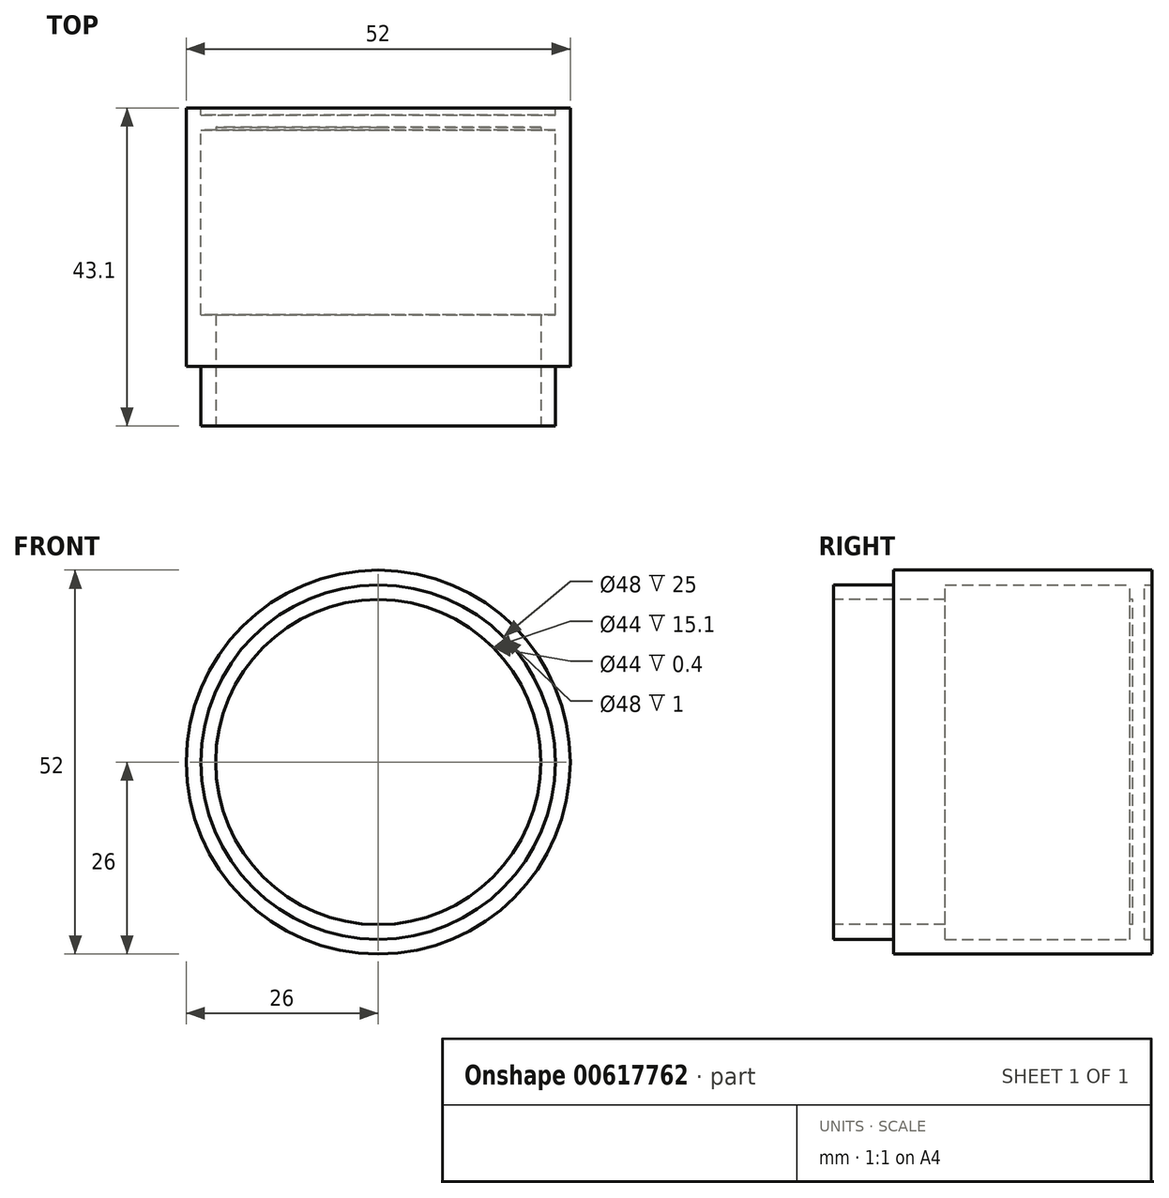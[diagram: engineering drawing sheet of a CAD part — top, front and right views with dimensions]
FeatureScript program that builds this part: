
annotation { "Feature Type Name" : "Feature", "Feature Type Description" : "" }
export const myFeature = defineFeature(function(context is Context, id is Id, definition is map)
    precondition{}
    {
        {
            var Q0;
            Q0=qCreatedBy(makeId("Front.planeOp"),FACE);
            var sketch = newSketch(context, id + "F0", { "sketchPlane" : qUnion([Q0])});
            skArc(sketch, "E0", {"start": v(-25.92, -2) * mm, "mid": v(0, -26) * mm, "end": v(25.92, -2) * mm});
            skCircle(sketch, "E1", {"center": v(0, 0) * mm, "radius": 24 * mm});
            skArc(sketch, "E2.trimOffspring", {"start": v(25.92, 2) * mm, "mid": v(0, 26) * mm, "end": v(-25.92, 2) * mm});
            skArc(sketch, "E3", {"start": v(25.92, -2) * mm, "mid": v(26, 0) * mm, "end": v(25.92, 2) * mm});
            skPoint(sketch, "E4.MirrorCS.end.orphan", {"position": v(26.83, -2) * mm});
            skPoint(sketch, "E4.MirrorCS.start.orphan", {"position": v(26.83, 2) * mm});
            skArc(sketch, "E5.trimOffspring", {"start": v(-25.92, 2) * mm, "mid": v(-26, 0) * mm, "end": v(-25.92, -2) * mm});
            skPoint(sketch, "E6.MirrorCS.start.orphan", {"position": v(-26.83, -2) * mm});
            skPoint(sketch, "E7.start.orphan", {"position": v(-26.83, 2) * mm});
            skCircle(sketch, "E8", {"center": v(0, 0) * mm, "radius": 22 * mm});
            skSolve(sketch);
        }
        {
            var Q0;
            Q0=makeQuery(id+"F0.imprint","IMPRINT",FACE,{"disambiguationData":[TD([[makeQuery(id+"F0.imprint","IMPRINT",EDGE,{"derivedFrom":sQuery(id+"F0.wireOp",EDGE,"E0")}),1.0]])]});
            extrude(context, id + "F1", {"entities" : qUnion([Q0]), "depth" : 35 * mm, "offsetDistance" : 25 * mm});
        }
        {
            var Q0;
            Q0=makeQuery(id+"F0.imprint","IMPRINT",FACE,{"disambiguationData":[TD([[makeQuery(id+"F0.imprint","IMPRINT",EDGE,{"derivedFrom":sQuery(id+"F0.wireOp",EDGE,"E1")}),1.0]])]});
            var Q1;
            Q1=makeQuery(id+"F0.imprint","IMPRINT",FACE,{"disambiguationData":[TD([[makeQuery(id+"F0.imprint","IMPRINT",EDGE,{"derivedFrom":sQuery(id+"F0.wireOp",EDGE,"E8")}),1.0]])]});
            extrude(context, id + "F2", {"entities" : qUnion([Q0, Q1]), "operationType" : NewBodyOperationType.ADD, "depth" : 3 * mm, "offsetDistance" : 25 * mm, "hasSecondDirection" : true, "secondDirectionOppositeDirection" : false, "secondDirectionDepth" : 1 * mm});
        }
        {
            var Q0;
            Q0=makeQuery(id+"F2.opExtrude","CAP_FACE",FACE,{"disambiguationData":[OSD([sQuery(id+"F0.wireOp",EDGE,"E1"),sQuery(id+"F0.wireOp",EDGE,"E8")])],"isStart":true});
            extrude(context, id + "F3", {"entities" : qUnion([Q0]), "operationType" : NewBodyOperationType.ADD, "oppositeDirection" : true, "depth" : 42.1 * mm, "offsetDistance" : 25 * mm, "hasSecondDirection" : true, "secondDirectionOppositeDirection" : true, "secondDirectionDepth" : 27 * mm});
        }
        {
            var Q0;
            Q0=makeQuery(id+"F3.opExtrude","CAP_FACE",FACE,{"disambiguationData":[OSD([sQuery(id+"F0.wireOp",EDGE,"E1")])],"isStart":false});
            var sketch = newSketch(context, id + "F4", { "sketchPlane" : qUnion([Q0])});
            skCircle(sketch, "E9", {"center": v(0, 0) * mm, "radius": 22 * mm});
            skSolve(sketch);
        }
        {
            var Q0;
            Q0 = qSketchRegion(id + "F4", true);
            extrude(context, id + "F5", {"entities" : qUnion([Q0]), "operationType" : NewBodyOperationType.REMOVE, "surfaceOperationType" : NewSurfaceOperationType.ADD, "oppositeDirection" : true, "depth" : 40.5 * mm, "offsetDistance" : 25 * mm});
        }
    });
